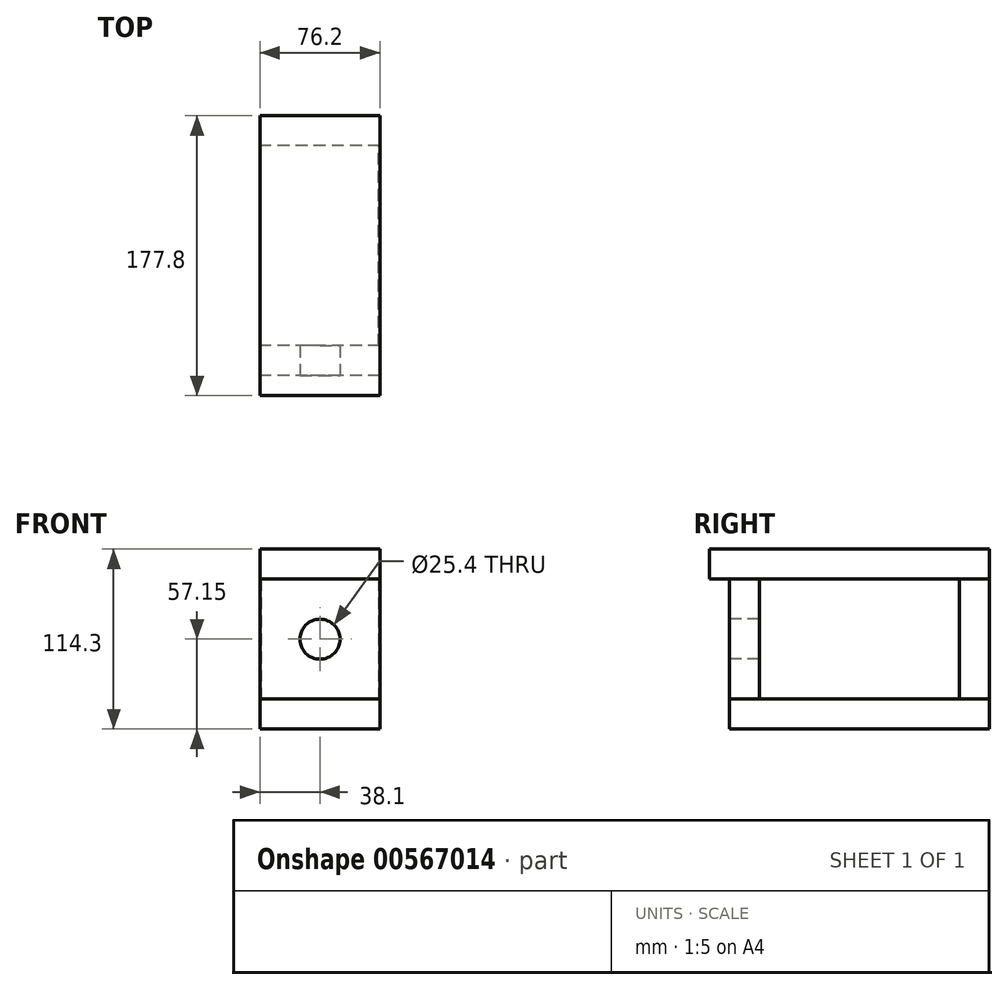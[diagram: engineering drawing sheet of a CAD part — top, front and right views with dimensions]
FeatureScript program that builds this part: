
annotation { "Feature Type Name" : "Feature", "Feature Type Description" : "" }
export const myFeature = defineFeature(function(context is Context, id is Id, definition is map)
    precondition{}
    {
        {
            assignVariable(context, id + "F0", {"name" : "thickness", "anyValue" : 0.75});
        }
        {
            var Q0;
            Q0=qCreatedBy(makeId("Right.planeOp"),FACE);
            var sketch = newSketch(context, id + "F1", { "sketchPlane" : qUnion([Q0])});
            skLineSegment(sketch, "E0.bottom", {"start": v(-95.25, 114.3) * mm, "end": v(82.55, 114.3) * mm});
            skLineSegment(sketch, "E0.top", {"start": v(-95.25, 95.25) * mm, "end": v(82.55, 95.25) * mm});
            skLineSegment(sketch, "E0.left", {"start": v(-95.25, 114.3) * mm, "end": v(-95.25, 95.25) * mm});
            skLineSegment(sketch, "E0.right", {"start": v(82.55, 114.3) * mm, "end": v(82.55, 95.25) * mm});
            skLineSegment(sketch, "E1.bottom", {"start": v(-82.55, 0) * mm, "end": v(82.55, 0) * mm});
            skLineSegment(sketch, "E1.top", {"start": v(-82.55, 19.05) * mm, "end": v(82.55, 19.05) * mm});
            skLineSegment(sketch, "E1.left", {"start": v(-82.55, 0) * mm, "end": v(-82.55, 19.05) * mm});
            skLineSegment(sketch, "E1.right", {"start": v(82.55, 0) * mm, "end": v(82.55, 19.05) * mm});
            skLineSegment(sketch, "E2.bottom", {"start": v(63.5, 95.25) * mm, "end": v(82.55, 95.25) * mm});
            skLineSegment(sketch, "E2.top", {"start": v(63.5, 19.05) * mm, "end": v(82.55, 19.05) * mm});
            skLineSegment(sketch, "E2.left", {"start": v(63.5, 95.25) * mm, "end": v(63.5, 19.05) * mm});
            skLineSegment(sketch, "E2.right", {"start": v(82.55, 95.25) * mm, "end": v(82.55, 19.05) * mm});
            skLineSegment(sketch, "E3.bottom", {"start": v(-82.55, 95.25) * mm, "end": v(-63.5, 95.25) * mm});
            skLineSegment(sketch, "E3.top", {"start": v(-82.55, 19.05) * mm, "end": v(-63.5, 19.05) * mm});
            skLineSegment(sketch, "E3.left", {"start": v(-82.55, 95.25) * mm, "end": v(-82.55, 19.05) * mm});
            skLineSegment(sketch, "E3.right", {"start": v(-63.5, 95.25) * mm, "end": v(-63.5, 19.05) * mm});
            skSolve(sketch);
        }
        {
            var Q0;
            Q0=makeQuery(id+"F1.imprint","IMPRINT",FACE,{"disambiguationData":[TD([[makeQuery(id+"F1.imprint","IMPRINT",EDGE,{"derivedFrom":sQuery(id+"F1.wireOp",EDGE,"E1.bottom")}),1.0]])]});
            extrude(context, id + "F2", {"entities" : qUnion([Q0]), "endBound" : BoundingType.SYMMETRIC, "depth" : 76.2 * mm, "offsetDistance" : 25.4 * mm});
        }
        {
            var Q0;
            {var subQ2=sQuery(id+"F1.wireOp",EDGE,"E2.left");Q0=makeQuery(id+"F1.imprint","IMPRINT",FACE,{"disambiguationData":[TD([[makeQuery(id+"F1.imprint","IMPRINT",EDGE,{"derivedFrom":subQ2}),1.0]])]});}
            extrude(context, id + "F3", {"entities" : qUnion([Q0]), "endBound" : BoundingType.SYMMETRIC, "depth" : 76.2 * mm, "offsetDistance" : 25.4 * mm});
        }
        {
            var Q0;
            Q0=makeQuery(id+"F1.imprint","IMPRINT",FACE,{"disambiguationData":[TD([[makeQuery(id+"F1.imprint","IMPRINT",EDGE,{"derivedFrom":sQuery(id+"F1.wireOp",EDGE,"E0.bottom")}),-1.0]])]});
            extrude(context, id + "F4", {"entities" : qUnion([Q0]), "endBound" : BoundingType.SYMMETRIC, "depth" : 76.2 * mm, "offsetDistance" : 25.4 * mm});
        }
        {
            var Q0;
            {var subQ2=sQuery(id+"F1.wireOp",EDGE,"E3.left");Q0=makeQuery(id+"F1.imprint","IMPRINT",FACE,{"disambiguationData":[TD([[makeQuery(id+"F1.imprint","IMPRINT",EDGE,{"derivedFrom":subQ2}),1.0]])]});}
            var Q1;
            Q1 = qSketchRegion(id + "F6", true);
            extrude(context, id + "F5", {"entities" : qUnion([Q0, Q1]), "endBound" : BoundingType.SYMMETRIC, "depth" : 76.2 * mm, "offsetDistance" : 25.4 * mm});
        }
        {
            var Q0;
            Q0=makeQuery(id+"F5.opExtrude","SWEPT_FACE",FACE,{"disambiguationData":[OSD([sQuery(id+"F1.wireOp",EDGE,"E3.left")])]});
            var sketch = newSketch(context, id + "F6", { "sketchPlane" : qUnion([Q0])});
            skCircle(sketch, "E4", {"center": v(0, 57.15) * mm, "radius": 12.7 * mm});
            skSolve(sketch);
        }
        {
            var Q0;
            Q0=makeQuery(id+"F6.imprint","IMPRINT",FACE,{"disambiguationData":[TD([[makeQuery(id+"F6.imprint","IMPRINT",EDGE,{"derivedFrom":sQuery(id+"F6.wireOp",EDGE,"E4")}),1.0]])]});
            var Q1;
            Q1=sQuery(id+"F6.wireOp",EDGE,"E4");
            extrude(context, id + "F7", {"entities" : qUnion([Q0]), "operationType" : NewBodyOperationType.REMOVE, "surfaceEntities" : qUnion([Q1]), "endBound" : BoundingType.UP_TO_NEXT, "oppositeDirection" : true, "depth" : 12.7 * mm, "offsetDistance" : 25.4 * mm});
        }
        {
            var Q0;
            Q0=makeQuery(id+"F2.opExtrude","CAP_FACE",FACE,{"disambiguationData":[OSD([sQuery(id+"F1.wireOp",EDGE,"E1.bottom"),sQuery(id+"F1.wireOp",EDGE,"E1.top"),sQuery(id+"F1.wireOp",EDGE,"E1.left"),sQuery(id+"F1.wireOp",EDGE,"E1.right")])],"isStart":true});
            var sketch = newSketch(context, id + "F8", { "sketchPlane" : qUnion([Q0])});
            skLineSegment(sketch, "E5.bottom", {"start": v(63.5, 95.25) * mm, "end": v(-63.5, 95.25) * mm});
            skLineSegment(sketch, "E5.top", {"start": v(63.5, 19.05) * mm, "end": v(-63.5, 19.05) * mm});
            skLineSegment(sketch, "E5.left", {"start": v(-63.5, 95.25) * mm, "end": v(-63.5, 19.05) * mm});
            skLineSegment(sketch, "E5.right", {"start": v(63.5, 95.25) * mm, "end": v(63.5, 19.05) * mm});
            skSolve(sketch);
        }
        {
            var Q0;
            Q0=makeQuery(id+"F8.imprint","IMPRINT",FACE,{"disambiguationData":[TD([[makeQuery(id+"F8.imprint","IMPRINT",EDGE,{"derivedFrom":sQuery(id+"F8.wireOp",EDGE,"E5.bottom")}),1.0]])]});
            extrude(context, id + "F9", {"entities" : qUnion([Q0]), "oppositeDirection" : true, "depth" : (getVariable(context, 'thickness')) * mm, "offsetDistance" : 25.4 * mm});
        }
        {
            var Q0;
            Q0=makeQuery(id+"F2.opExtrude","CAP_FACE",FACE,{"disambiguationData":[OSD([sQuery(id+"F1.wireOp",EDGE,"E1.bottom"),sQuery(id+"F1.wireOp",EDGE,"E1.top"),sQuery(id+"F1.wireOp",EDGE,"E1.left"),sQuery(id+"F1.wireOp",EDGE,"E1.right")])],"isStart":false});
            var sketch = newSketch(context, id + "F10", { "sketchPlane" : qUnion([Q0])});
            skLineSegment(sketch, "E6.0.0", {"start": v(-63.5, 95.25) * mm, "end": v(-63.5, 19.05) * mm});
            skLineSegment(sketch, "E6.0.1", {"start": v(-63.5, 19.05) * mm, "end": v(63.5, 19.05) * mm});
            skLineSegment(sketch, "E6.0.2", {"start": v(63.5, 19.05) * mm, "end": v(63.5, 95.25) * mm});
            skLineSegment(sketch, "E6.0.3", {"start": v(63.5, 95.25) * mm, "end": v(-63.5, 95.25) * mm});
            skSolve(sketch);
        }
        {
            var Q0;
            Q0=makeQuery(id+"F10.imprint","IMPRINT",FACE,{"disambiguationData":[TD([[makeQuery(id+"F10.imprint","IMPRINT",EDGE,{"derivedFrom":sQuery(id+"F10.wireOp",EDGE,"E6.0.0")}),1.0]])]});
            extrude(context, id + "F11", {"entities" : qUnion([Q0]), "oppositeDirection" : true, "depth" : (getVariable(context, 'thickness')) * mm, "offsetDistance" : 25.4 * mm});
        }
        {
            var Q0;
            Q0=makeQuery(id+"F11.opExtrude","CAP_EDGE",EDGE,{"disambiguationData":[OSD([sQuery(id+"F10.wireOp",EDGE,"E6.0.3")])],"isStart":true});
            var Q1;
            Q1=makeQuery(id+"F11.opExtrude","CAP_EDGE",EDGE,{"disambiguationData":[OSD([sQuery(id+"F10.wireOp",EDGE,"E6.0.1")])],"isStart":false});
            fillet(context, id + "F12", {"entities" : qUnion([Q0, Q1]), "radius" : (getVariable(context, 'thickness')) * mm, "tangentPropagation" : true, "allowEdgeOverflow" : false});
        }
        {
            var Q0;
            Q0=makeQuery(id+"F11.opExtrude","SWEPT_FACE",FACE,{"disambiguationData":[OSD([sQuery(id+"F10.wireOp",EDGE,"E6.0.0")])]});
            var sketch = newSketch(context, id + "F13", { "sketchPlane" : qUnion([Q0])});
            skPoint(sketch, "E7", {"position": v(28.58, 85.72) * mm});
            skSolve(sketch);
        }
    });
